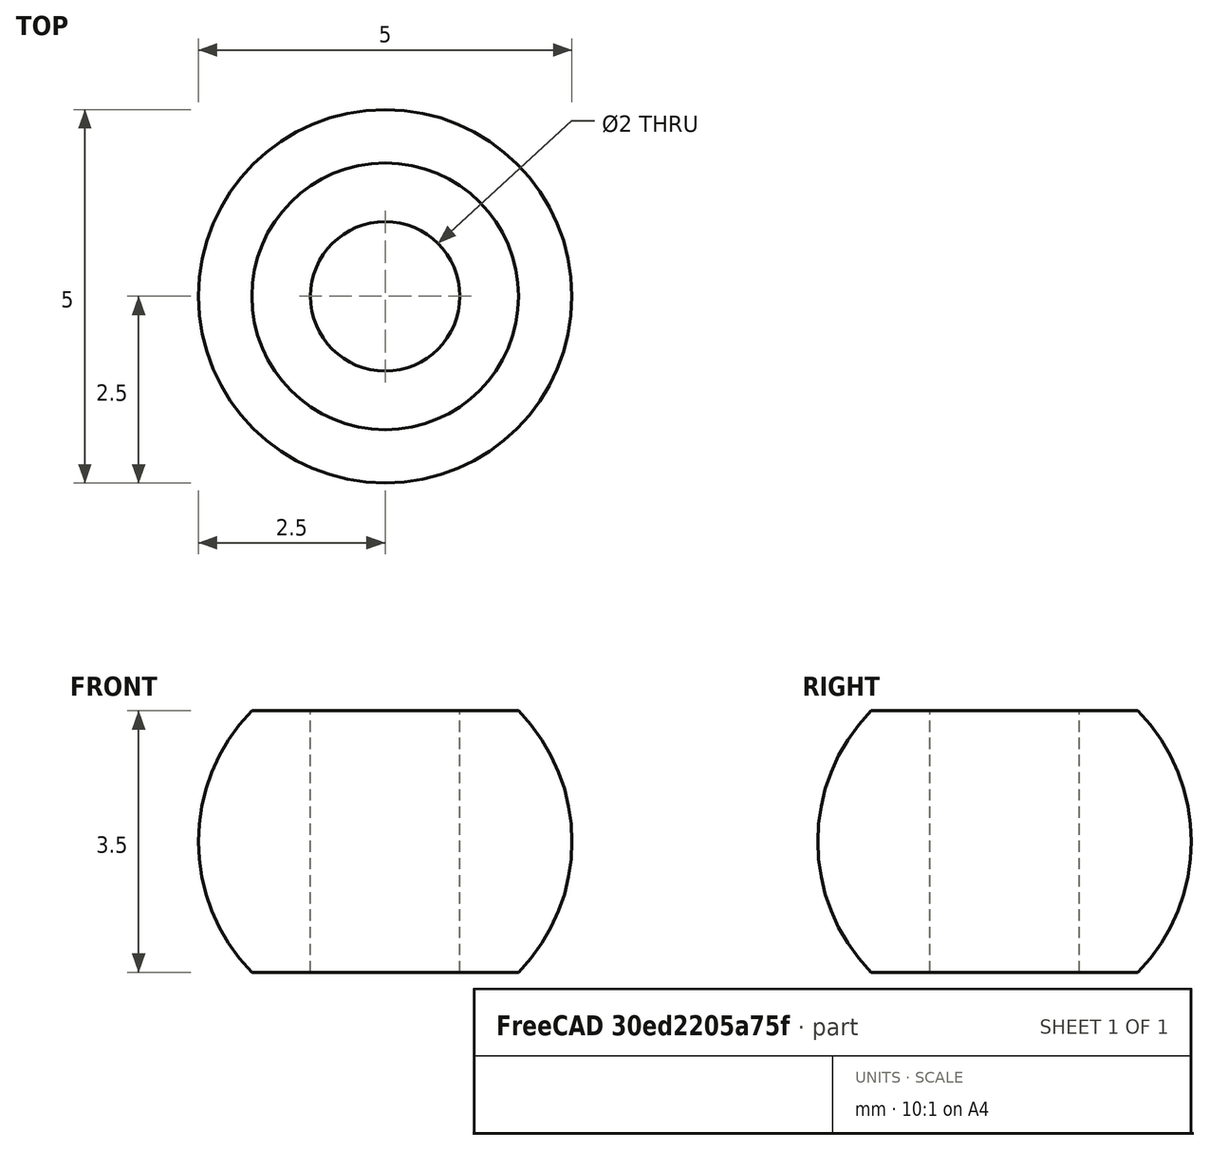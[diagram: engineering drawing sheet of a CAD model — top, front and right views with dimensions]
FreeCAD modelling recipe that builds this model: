
FCSTD DOCUMENT  (FreeCAD 1.0R39109 (Git))
Label: M2RodEndBall
License: All rights reserved
LicenseURL: http://en.wikipedia.org/wiki/All_rights_reserved
objects: Sketcher::SketchObject×1, PartDesign::Revolution×1, PartDesign::Body×1, App::Link×1
note: 6 computed .brp shape members not serialized (recipe doc carries the construction recipe); baked Part::Feature solids carry a one-line shape summary decoded from their .brp
EXTERNAL_REF file=../../Dimentions.FCStd obj=dd

FEATURE [Sketcher::SketchObject] Sketch
  ArcFitTolerance = 1e-06
  AttachmentSupport = -> [YZ_Plane]
  FullyConstrained = true
  MakeInternals = false
  MapMode = 5
  Placement = pos=(0,0,0) rot=(0.57735,0.57735,0.57735;2.0944rad)
  expr: .Constraints.BallDiameter = <<M2RodEnd>>.BallDiameter
  expr: .Constraints.BallThickness = <<M2RodEnd>>.BallThickness
  expr: .Constraints.HoleDiameter = <<M2RodEnd>>.HoleDiameter
  sketch-geometry (10):
    g0: LineSegment StartX=1 StartY=1.75 StartZ=0 EndX=1.78536 EndY=1.75 EndZ=0
    g1: LineSegment [constr] StartX=1.78536 StartY=1.75 StartZ=0 EndX=1.78536 EndY=-1.75 EndZ=0
    g2: LineSegment StartX=1.78536 StartY=-1.75 StartZ=0 EndX=1 EndY=-1.75 EndZ=0
    g3: LineSegment StartX=1 StartY=-1.75 StartZ=0 EndX=1 EndY=1.75 EndZ=0
    g4: LineSegment [constr] StartX=-1 StartY=1.75 StartZ=0 EndX=-1.78536 EndY=1.75 EndZ=0
    g5: LineSegment [constr] StartX=-1.78536 StartY=1.75 StartZ=0 EndX=-1.78536 EndY=-1.75 EndZ=0
    g6: LineSegment [constr] StartX=-1.78536 StartY=-1.75 StartZ=0 EndX=-1 EndY=-1.75 EndZ=0
    g7: ArcOfCircle CenterX=0 CenterY=0 CenterZ=0 NormalX=0 NormalY=0 NormalZ=1 AngleXU=0 Radius=2.5 StartAngle=5.50779 EndAngle=7.05858
    g8: ArcOfCircle [constr] CenterX=0 CenterY=0 CenterZ=0 NormalX=0 NormalY=0 NormalZ=1 AngleXU=0 Radius=2.5 StartAngle=2.3662 EndAngle=3.91699
    g9: LineSegment [constr] StartX=-1 StartY=-1.75 StartZ=0 EndX=-1 EndY=1.75 EndZ=0
  constraints (26):
    c: Coincident(g0,g1)
    c: Coincident(g1,g2)
    c: Horizontal(g0)
    c: Horizontal(g2)
    c: Symmetric(g2,g0,g-1)
    c: Coincident(g4,g5)
    c: Coincident(g5,g6)
    c: Horizontal(g4)
    c: Horizontal(g6)
    c: Equal(g6,g2)
    c: Vertical(g5)
    c: Coincident(g7,g-1)
    c: Coincident(g8,g7)
    c: Diameter(g7) = 5  'BallDiameter'
    c: Coincident(g7,g0)
    c: Coincident(g2,g7)
    c: Coincident(g8,g5)
    c: Symmetric(g4,g0,g-2)
    c: Coincident(g3,g0)
    c: Coincident(g8,g4)
    c: Coincident(g3,g2)
    c: Equal(g4,g0)
    c: DistanceX(g4,g0) = 2  'HoleDiameter'
    c: Coincident(g9,g6)
    c: Coincident(g9,g4)
    c: DistanceY(g2,g0) = 3.5  'BallThickness'
FEATURE [PartDesign::Revolution] Revolution
  Angle = 360
  Angle2 = 60
  Axis = (0,0,1)
  Base = (0,0,0)
  Placement = pos=(0,0,0) rot=(0.57735,0.57735,0.57735;2.0944rad)
  Profile = -> Sketch
  ReferenceAxis = -> Sketch [V_Axis]
  Reversed = true
  Suppressed = false
  Type = 0
FEATURE [PartDesign::Body] Body  label="RodEndBall"
  AllowCompound = false
  Group = -> [Sketch,Revolution]
  Origin = -> Origin
  Tip = -> Revolution
FEATURE [App::Link] Link001  label="M2RodEnd"
  LinkedObject = -> <external ../../Dimentions.FCStd>#dd
